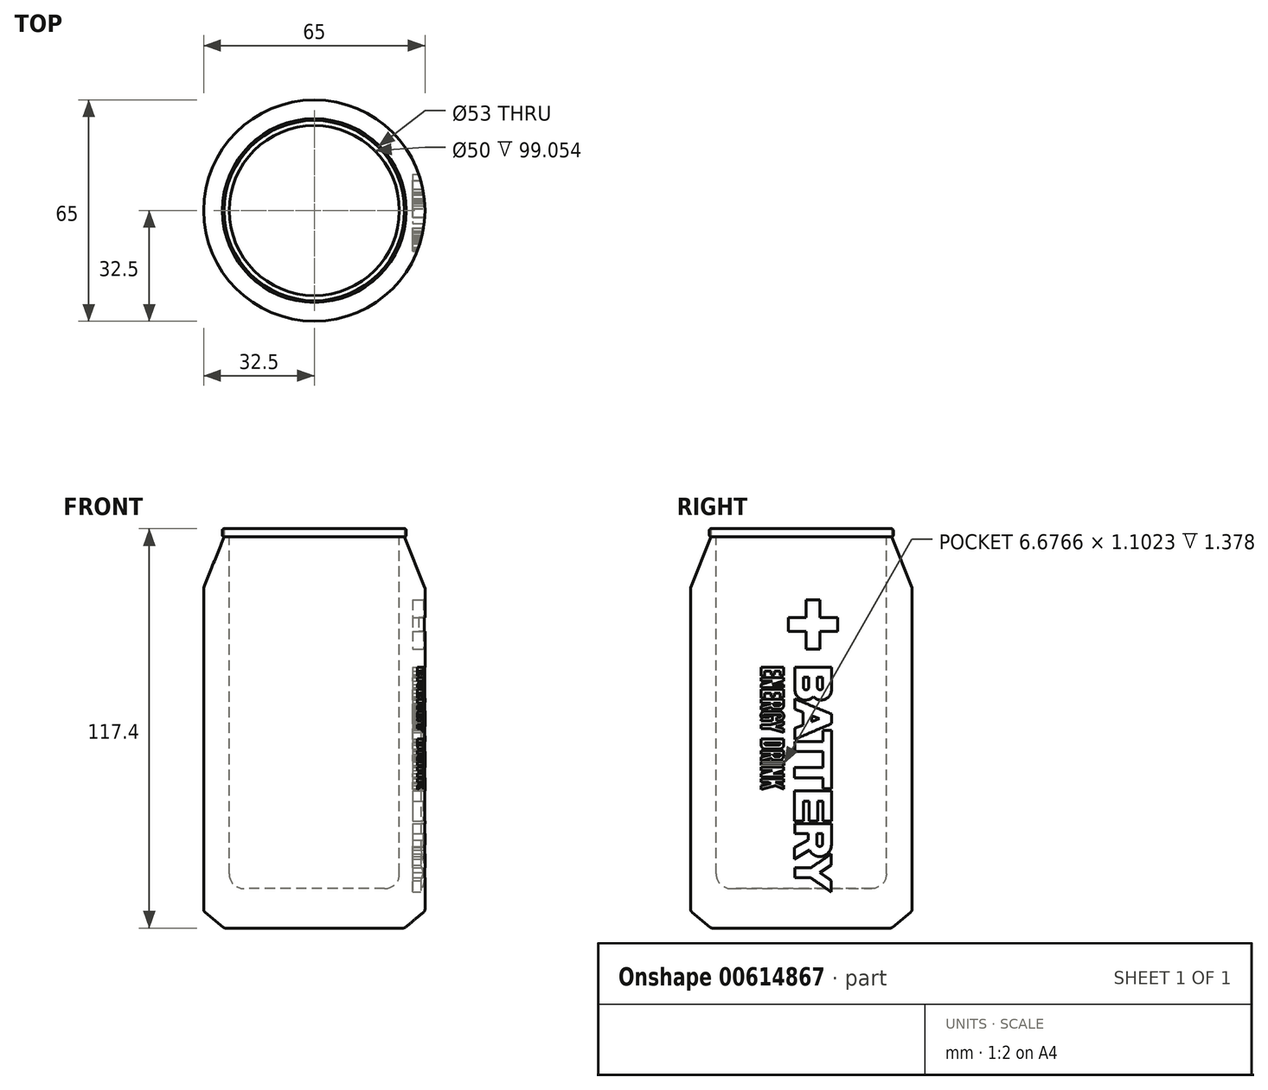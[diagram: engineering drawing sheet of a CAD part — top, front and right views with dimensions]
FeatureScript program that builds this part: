
annotation { "Feature Type Name" : "Feature", "Feature Type Description" : "" }
export const myFeature = defineFeature(function(context is Context, id is Id, definition is map)
    precondition{}
    {
        {
            var Q0;
            Q0=qCreatedBy(makeId("Top.planeOp"),FACE);
            var sketch = newSketch(context, id + "F0", { "sketchPlane" : qUnion([Q0])});
            skCircle(sketch, "E0", {"center": v(0, 0) * mm, "radius": 32.5 * mm});
            skSolve(sketch);
        }
        {
            var Q0;
            Q0=makeQuery(id+"F0.imprint","IMPRINT",FACE,{"disambiguationData":[TD([[makeQuery(id+"F0.imprint","IMPRINT",EDGE,{"derivedFrom":sQuery(id+"F0.wireOp",EDGE,"E0")}),1.0]])]});
            extrude(context, id + "F1", {"entities" : qUnion([Q0]), "depth" : 115 * mm, "offsetDistance" : 25 * mm});
        }
        {
            var Q0;
            Q0=makeQuery(id+"F1.opExtrude","CAP_FACE",FACE,{"disambiguationData":[OSD([sQuery(id+"F0.wireOp",EDGE,"E0")])],"isStart":true});
            chamfer(context, id + "F2", {"entities" : qUnion([Q0]), "chamferType" : ChamferType.TWO_OFFSETS, "width1" : 5 * mm, "oppositeDirection" : false, "width2" : 6 * mm, "tangentPropagation" : true});
        }
        {
            var Q0;
            {var subQ0=sQuery(id+"F0.wireOp",EDGE,"E0");Q0=makeQuery(id+"F2.opChamfer","BLEND_EDGE",EDGE,{"blendedFrom":[makeQuery(id+"F1.opExtrude","CAP_EDGE",EDGE,{"disambiguationData":[OSD([subQ0])],"isStart":true}),makeQuery(id+"F1.opExtrude","SWEPT_FACE",FACE,{"disambiguationData":[OSD([subQ0])]})],"blendedInto":[makeQuery(id+"F1.opExtrude","SWEPT_FACE",FACE,{"disambiguationData":[OSD([subQ0])]})]});}
            var Q1;
            {var subQ0=sQuery(id+"F0.wireOp",EDGE,"E0");Q1=makeQuery(id+"F2.opChamfer","BLEND_EDGE",EDGE,{"blendedFrom":[makeQuery(id+"F1.opExtrude","CAP_EDGE",EDGE,{"disambiguationData":[OSD([subQ0])],"isStart":true}),makeQuery(id+"F1.opExtrude","CAP_FACE",FACE,{"disambiguationData":[OSD([subQ0])],"isStart":true})],"blendedInto":[makeQuery(id+"F1.opExtrude","CAP_FACE",FACE,{"disambiguationData":[OSD([subQ0])],"isStart":true})]});}
            fillet(context, id + "F3", {"entities" : qUnion([Q0, Q1]), "radius" : 1.04 * mm, "tangentPropagation" : true, "allowEdgeOverflow" : false});
        }
        {
            var Q0;
            Q0=makeQuery(id+"F1.opExtrude","CAP_FACE",FACE,{"disambiguationData":[OSD([sQuery(id+"F0.wireOp",EDGE,"E0")])],"isStart":false});
            chamfer(context, id + "F4", {"entities" : qUnion([Q0]), "chamferType" : ChamferType.TWO_OFFSETS, "width1" : 6 * mm, "oppositeDirection" : false, "width2" : 15 * mm, "tangentPropagation" : true});
        }
        {
            var Q0;
            Q0=makeQuery(id+"F1.opExtrude","CAP_FACE",FACE,{"disambiguationData":[OSD([sQuery(id+"F0.wireOp",EDGE,"E0")])],"isStart":false});
            var sketch = newSketch(context, id + "F5", { "sketchPlane" : qUnion([Q0])});
            skCircle(sketch, "E1", {"center": v(0, 0) * mm, "radius": 25 * mm});
            skSolve(sketch);
        }
        {
            var Q0;
            Q0=makeQuery(id+"F5.imprint","IMPRINT",FACE,{"disambiguationData":[TD([[makeQuery(id+"F5.imprint","IMPRINT",EDGE,{"derivedFrom":sQuery(id+"F5.wireOp",EDGE,"E1")}),1.0]])]});
            extrude(context, id + "F6", {"entities" : qUnion([Q0]), "operationType" : NewBodyOperationType.REMOVE, "oppositeDirection" : true, "depth" : 103.4 * mm, "offsetDistance" : 25 * mm});
        }
        {
            var Q0;
            Q0=makeQuery(id+"F1.opExtrude","CAP_FACE",FACE,{"disambiguationData":[OSD([sQuery(id+"F0.wireOp",EDGE,"E0")])],"isStart":false});
            var sketch = newSketch(context, id + "F7", { "sketchPlane" : qUnion([Q0])});
            skCircle(sketch, "E2", {"center": v(0, 0) * mm, "radius": 27 * mm});
            skSolve(sketch);
        }
        {
            var Q0;
            Q0=makeQuery(id+"F7.imprint","IMPRINT",FACE,{"disambiguationData":[TD([[makeQuery(id+"F7.imprint","IMPRINT",EDGE,{"derivedFrom":sQuery(id+"F7.wireOp",EDGE,"E2")}),1.0]])]});
            var Q1;
            Q1=makeQuery(id+"F7.imprint","IMPRINT",FACE,{"disambiguationData":[TD([[makeQuery(id+"F7.imprint","IMPRINT",EDGE,{"derivedFrom":makeQuery(id+"F6.boolean.opBoolean","COPY",EDGE,{"derivedFrom":makeQuery(id+"F6.opExtrude","CAP_EDGE",EDGE,{"disambiguationData":[OSD([sQuery(id+"F5.wireOp",EDGE,"E1")])],"isStart":true})})}),-1.0]])]});
            extrude(context, id + "F8", {"entities" : qUnion([Q0, Q1]), "operationType" : NewBodyOperationType.ADD, "depth" : 2.4 * mm, "offsetDistance" : 25 * mm});
        }
        {
            var Q0;
            Q0=makeQuery(id+"F8.opExtrude","SWEPT_FACE",FACE,{"disambiguationData":[OSD([sQuery(id+"F7.wireOp",EDGE,"E2")])]});
            var Q1;
            Q1=makeQuery(id+"F8.opExtrude","CAP_EDGE",EDGE,{"disambiguationData":[OSD([sQuery(id+"F5.wireOp",EDGE,"E1")])],"isStart":false});
            var Q2;
            {var subQ0=sQuery(id+"F0.wireOp",EDGE,"E0");Q2=makeQuery(id+"F4.opChamfer","BLEND_EDGE",EDGE,{"blendedFrom":[makeQuery(id+"F1.opExtrude","CAP_EDGE",EDGE,{"disambiguationData":[OSD([subQ0])],"isStart":false}),makeQuery(id+"F1.opExtrude","SWEPT_FACE",FACE,{"disambiguationData":[OSD([subQ0])]})],"blendedInto":[makeQuery(id+"F1.opExtrude","SWEPT_FACE",FACE,{"disambiguationData":[OSD([subQ0])]})]});}
            fillet(context, id + "F9", {"entities" : qUnion([Q0, Q1, Q2]), "radius" : .5 * mm, "tangentPropagation" : true, "allowEdgeOverflow" : false});
        }
        {
            var Q0;
            Q0=qCreatedBy(makeId("Right.planeOp"),FACE);
            cPlane(context, id + "F10", {"entities" : qUnion([Q0]), "cplaneType" : CPlaneType.OFFSET, "offset" : 41.2 * mm, "width" : 150 * mm, "height" : 150 * mm});
        }
        {
            var Q0;
            Q0=qCreatedBy(id+"F10.planeOp",FACE);
            var sketch = newSketch(context, id + "F11", { "sketchPlane" : qUnion([Q0])});
            skLineSegment(sketch, "E3", {"start": v(-9.72, 42.86) * mm, "end": v(-11.78, 42.86) * mm});
            skLineSegment(sketch, "E4", {"start": v(-5.14, 41.9) * mm, "end": v(-7.6, 42.86) * mm});
            skLineSegment(sketch, "E5", {"start": v(-5.14, 40.87) * mm, "end": v(-5.14, 41.9) * mm});
            skLineSegment(sketch, "E6", {"start": v(-7.6, 41.85) * mm, "end": v(-5.14, 40.87) * mm});
            skLineSegment(sketch, "E7", {"start": v(-11.8, 40.77) * mm, "end": v(-7.6, 41.85) * mm});
            skLineSegment(sketch, "E8", {"start": v(-11.8, 41.83) * mm, "end": v(-11.8, 40.77) * mm});
            skLineSegment(sketch, "E9", {"start": v(-5.18, 67.76) * mm, "end": v(-6.17, 67.76) * mm});
            skLineSegment(sketch, "E10", {"start": v(-6.17, 69.09) * mm, "end": v(-6.17, 67.76) * mm});
            skLineSegment(sketch, "E11", {"start": v(-5.18, 69.09) * mm, "end": v(-5.18, 67.76) * mm});
            skLineSegment(sketch, "E12", {"start": v(-10.8, 69.09) * mm, "end": v(-8.85, 69.09) * mm});
            skLineSegment(sketch, "E13", {"start": v(-11.82, 70.2) * mm, "end": v(-5.18, 70.2) * mm});
            skLineSegment(sketch, "E14", {"start": v(-5.18, 70.2) * mm, "end": v(-5.18, 69.09) * mm});
            skLineSegment(sketch, "E15", {"start": v(-11.82, 70.2) * mm, "end": v(-11.82, 69.09) * mm});
            skLineSegment(sketch, "E16", {"start": v(-7.83, 75.55) * mm, "end": v(-6.2, 75.55) * mm});
            skLineSegment(sketch, "E17", {"start": v(-11.8, 71.6) * mm, "end": v(-8.5, 72.66) * mm});
            skLineSegment(sketch, "E18", {"start": v(-5.2, 72.66) * mm, "end": v(-8.5, 71.6) * mm});
            skLineSegment(sketch, "E19", {"start": v(-5.2, 70.67) * mm, "end": v(-11.8, 70.67) * mm});
            skLineSegment(sketch, "E20", {"start": v(-5.2, 71.6) * mm, "end": v(-8.5, 71.6) * mm});
            skLineSegment(sketch, "E21", {"start": v(-11.8, 71.6) * mm, "end": v(-11.8, 70.67) * mm});
            skLineSegment(sketch, "E22", {"start": v(-5.2, 71.6) * mm, "end": v(-5.2, 70.67) * mm});
            skLineSegment(sketch, "E23", {"start": v(-11.8, 73.6) * mm, "end": v(-5.2, 73.6) * mm});
            skLineSegment(sketch, "E24", {"start": v(-11.8, 72.66) * mm, "end": v(-8.5, 72.66) * mm});
            skLineSegment(sketch, "E25", {"start": v(-5.2, 72.66) * mm, "end": v(-5.2, 73.6) * mm});
            skLineSegment(sketch, "E26", {"start": v(-11.8, 72.66) * mm, "end": v(-11.8, 73.6) * mm});
            skLineSegment(sketch, "E27", {"start": v(-10.82, 74.14) * mm, "end": v(-11.82, 74.14) * mm});
            skLineSegment(sketch, "E28", {"start": v(-11.82, 75.55) * mm, "end": v(-11.82, 74.14) * mm});
            skLineSegment(sketch, "E29", {"start": v(-10.82, 75.55) * mm, "end": v(-10.82, 74.14) * mm});
            skLineSegment(sketch, "E30", {"start": v(-7.83, 74.54) * mm, "end": v(-8.85, 74.54) * mm});
            skLineSegment(sketch, "E31", {"start": v(-8.85, 75.55) * mm, "end": v(-8.85, 74.54) * mm});
            skLineSegment(sketch, "E32", {"start": v(-7.83, 75.55) * mm, "end": v(-7.83, 74.54) * mm});
            skLineSegment(sketch, "E33", {"start": v(-5.16, 74.18) * mm, "end": v(-6.2, 74.18) * mm});
            skLineSegment(sketch, "E34", {"start": v(-6.2, 75.55) * mm, "end": v(-6.2, 74.18) * mm});
            skLineSegment(sketch, "E35", {"start": v(-5.16, 75.55) * mm, "end": v(-5.16, 74.18) * mm});
            skLineSegment(sketch, "E36", {"start": v(-10.82, 75.55) * mm, "end": v(-8.85, 75.55) * mm});
            skLineSegment(sketch, "E37", {"start": v(-11.82, 76.67) * mm, "end": v(-5.16, 76.67) * mm});
            skLineSegment(sketch, "E38", {"start": v(-5.16, 76.67) * mm, "end": v(-5.16, 75.55) * mm});
            skLineSegment(sketch, "E39", {"start": v(-11.82, 76.67) * mm, "end": v(-11.82, 75.55) * mm});
            skLineSegment(sketch, "E40", {"start": v(8.83, 10.61) * mm, "end": v(2.77, 14.79) * mm});
            skLineSegment(sketch, "E41", {"start": v(8.83, 13.98) * mm, "end": v(8.83, 10.61) * mm});
            skLineSegment(sketch, "E42", {"start": v(5.42, 16.3) * mm, "end": v(8.83, 13.98) * mm});
            skLineSegment(sketch, "E43", {"start": v(8.82, 18.56) * mm, "end": v(5.42, 16.3) * mm});
            skLineSegment(sketch, "E44", {"start": v(8.82, 21.8) * mm, "end": v(8.82, 18.56) * mm});
            skLineSegment(sketch, "E45", {"start": v(2.77, 17.7) * mm, "end": v(8.82, 21.8) * mm});
            skLineSegment(sketch, "E46", {"start": v(-1.93, 14.79) * mm, "end": v(2.77, 14.79) * mm});
            skLineSegment(sketch, "E47", {"start": v(-1.93, 17.7) * mm, "end": v(2.77, 17.7) * mm});
            skLineSegment(sketch, "E48", {"start": v(-1.93, 17.7) * mm, "end": v(-1.93, 14.79) * mm});
            skLineSegment(sketch, "E49", {"start": v(4.8, 37.31) * mm, "end": v(6.33, 37.31) * mm});
            skLineSegment(sketch, "E50", {"start": v(2.04, 27.75) * mm, "end": v(-1.92, 27.75) * mm});
            skArc(sketch, "E51", {"start": v(2.36, 22.94) * mm, "mid": v(6.22, 21.13) * mm, "end": v(8.86, 24.47) * mm});
            skArc(sketch, "E52", {"start": v(4.57, 24.84) * mm, "mid": v(5.42, 23.99) * mm, "end": v(6.28, 24.84) * mm});
            skLineSegment(sketch, "E53", {"start": v(8.86, 27.75) * mm, "end": v(8.86, 24.47) * mm});
            skLineSegment(sketch, "E54", {"start": v(6.28, 27.75) * mm, "end": v(6.28, 24.84) * mm});
            skLineSegment(sketch, "E55", {"start": v(4.57, 27.75) * mm, "end": v(4.57, 24.84) * mm});
            skLineSegment(sketch, "E56", {"start": v(-1.98, 20.3) * mm, "end": v(2.36, 22.94) * mm});
            skLineSegment(sketch, "E57", {"start": v(-1.98, 23.66) * mm, "end": v(-1.98, 20.3) * mm});
            skLineSegment(sketch, "E58", {"start": v(2.04, 25.9) * mm, "end": v(-1.98, 23.66) * mm});
            skLineSegment(sketch, "E59", {"start": v(6.3, 54.86) * mm, "end": v(-1.94, 54.86) * mm});
            skLineSegment(sketch, "E60", {"start": v(-1.94, 54.86) * mm, "end": v(-1.94, 51.9) * mm});
            skLineSegment(sketch, "E61", {"start": v(8.85, 40.97) * mm, "end": v(6.3, 40.97) * mm});
            skLineSegment(sketch, "E62", {"start": v(8.85, 58.09) * mm, "end": v(6.3, 58.09) * mm});
            skLineSegment(sketch, "E63", {"start": v(6.3, 58.09) * mm, "end": v(6.3, 54.86) * mm});
            skLineSegment(sketch, "E64", {"start": v(8.85, 58.09) * mm, "end": v(8.85, 40.97) * mm});
            skLineSegment(sketch, "E65", {"start": v(5.34, 61.55) * mm, "end": v(3.05, 62.44) * mm});
            skLineSegment(sketch, "E66", {"start": v(3.05, 60.66) * mm, "end": v(5.34, 61.55) * mm});
            skLineSegment(sketch, "E67", {"start": v(3.05, 62.44) * mm, "end": v(3.05, 60.66) * mm});
            skLineSegment(sketch, "E68", {"start": v(8.86, 62.9) * mm, "end": v(-1.9, 67.38) * mm});
            skLineSegment(sketch, "E69", {"start": v(8.86, 60.1) * mm, "end": v(8.86, 62.9) * mm});
            skLineSegment(sketch, "E70", {"start": v(-1.9, 55.48) * mm, "end": v(8.86, 60.1) * mm});
            skLineSegment(sketch, "E71", {"start": v(2.16, 73.7) * mm, "end": v(2.16, 70.77) * mm});
            skLineSegment(sketch, "E72", {"start": v(0.63, 73.7) * mm, "end": v(0.63, 70.77) * mm});
            skLineSegment(sketch, "E73", {"start": v(2.16, 73.7) * mm, "end": v(0.63, 73.7) * mm});
            skArc(sketch, "E74", {"start": v(4.76, 70.77) * mm, "mid": v(5.52, 70.01) * mm, "end": v(6.28, 70.77) * mm});
            skArc(sketch, "E75", {"start": v(0.63, 70.77) * mm, "mid": v(1.4, 70.01) * mm, "end": v(2.16, 70.77) * mm});
            skLineSegment(sketch, "E76", {"start": v(-1.9, 67.38) * mm, "end": v(-1.9, 64.33) * mm});
            skLineSegment(sketch, "E77", {"start": v(-1.9, 64.33) * mm, "end": v(0.48, 63.44) * mm});
            skLineSegment(sketch, "E78", {"start": v(0.48, 63.44) * mm, "end": v(0.48, 59.66) * mm});
            skLineSegment(sketch, "E79", {"start": v(0.48, 59.66) * mm, "end": v(-1.9, 58.7) * mm});
            skLineSegment(sketch, "E80", {"start": v(-1.9, 58.7) * mm, "end": v(-1.9, 55.48) * mm});
            skLineSegment(sketch, "E81", {"start": v(6.3, 51.9) * mm, "end": v(-1.94, 51.9) * mm});
            skLineSegment(sketch, "E82", {"start": v(-1.98, 47.19) * mm, "end": v(-1.98, 44.2) * mm});
            skLineSegment(sketch, "E83", {"start": v(6.3, 47.19) * mm, "end": v(-1.98, 47.19) * mm});
            skLineSegment(sketch, "E84", {"start": v(6.3, 44.2) * mm, "end": v(-1.98, 44.2) * mm});
            skLineSegment(sketch, "E85", {"start": v(6.3, 51.9) * mm, "end": v(6.3, 47.19) * mm});
            skLineSegment(sketch, "E86", {"start": v(6.3, 44.2) * mm, "end": v(6.3, 40.97) * mm});
            skLineSegment(sketch, "E87", {"start": v(-1.98, 40.28) * mm, "end": v(-1.98, 37.31) * mm});
            skLineSegment(sketch, "E88", {"start": v(8.85, 40.28) * mm, "end": v(8.85, 37.31) * mm});
            skLineSegment(sketch, "E89", {"start": v(-1.98, 40.28) * mm, "end": v(8.85, 40.28) * mm});
            skLineSegment(sketch, "E90", {"start": v(0.6, 37.31) * mm, "end": v(2.25, 37.31) * mm});
            skLineSegment(sketch, "E91", {"start": v(8.85, 37.31) * mm, "end": v(8.85, 31.42) * mm});
            skLineSegment(sketch, "E92", {"start": v(6.33, 37.31) * mm, "end": v(6.33, 31.42) * mm});
            skLineSegment(sketch, "E93", {"start": v(8.85, 31.42) * mm, "end": v(6.33, 31.42) * mm});
            skLineSegment(sketch, "E94", {"start": v(4.8, 37.31) * mm, "end": v(4.8, 31.42) * mm});
            skLineSegment(sketch, "E95", {"start": v(2.25, 37.31) * mm, "end": v(2.25, 31.42) * mm});
            skLineSegment(sketch, "E96", {"start": v(4.8, 31.42) * mm, "end": v(2.25, 31.42) * mm});
            skLineSegment(sketch, "E97", {"start": v(0.6, 37.31) * mm, "end": v(0.6, 31.43) * mm});
            skLineSegment(sketch, "E98", {"start": v(-1.98, 37.31) * mm, "end": v(-1.98, 31.43) * mm});
            skLineSegment(sketch, "E99", {"start": v(0.6, 31.43) * mm, "end": v(-1.98, 31.43) * mm});
            skLineSegment(sketch, "E100", {"start": v(8.86, 30.65) * mm, "end": v(8.86, 27.75) * mm});
            skLineSegment(sketch, "E101", {"start": v(-1.92, 30.65) * mm, "end": v(-1.92, 27.75) * mm});
            skLineSegment(sketch, "E102", {"start": v(8.86, 30.65) * mm, "end": v(-1.92, 30.65) * mm});
            skLineSegment(sketch, "E103", {"start": v(6.28, 27.75) * mm, "end": v(4.57, 27.75) * mm});
            skLineSegment(sketch, "E104", {"start": v(2.04, 27.75) * mm, "end": v(2.04, 25.9) * mm});
            skLineSegment(sketch, "E105", {"start": v(-7.8, 69.09) * mm, "end": v(-7.8, 68.04) * mm});
            skLineSegment(sketch, "E106", {"start": v(-8.85, 69.09) * mm, "end": v(-8.85, 68.04) * mm});
            skLineSegment(sketch, "E107", {"start": v(-7.8, 68.04) * mm, "end": v(-8.85, 68.04) * mm});
            skLineSegment(sketch, "E108", {"start": v(-10.8, 69.09) * mm, "end": v(-10.8, 67.65) * mm});
            skLineSegment(sketch, "E109", {"start": v(-11.82, 69.13) * mm, "end": v(-11.82, 67.65) * mm});
            skLineSegment(sketch, "E110", {"start": v(-10.8, 67.65) * mm, "end": v(-11.82, 67.65) * mm});
            skLineSegment(sketch, "E111", {"start": v(-7.8, 69.09) * mm, "end": v(-6.17, 69.09) * mm});
            skLineSegment(sketch, "E112", {"start": v(-11.8, 67.21) * mm, "end": v(-11.8, 66.13) * mm});
            skLineSegment(sketch, "E113", {"start": v(-5.19, 67.21) * mm, "end": v(-5.19, 66.13) * mm});
            skLineSegment(sketch, "E114", {"start": v(-11.8, 67.21) * mm, "end": v(-5.19, 67.21) * mm});
            skLineSegment(sketch, "E115", {"start": v(-11.8, 66.13) * mm, "end": v(-9.06, 66.13) * mm});
            skLineSegment(sketch, "E116", {"start": v(-9.06, 66.13) * mm, "end": v(-9.06, 65.87) * mm});
            skLineSegment(sketch, "E117", {"start": v(-9.06, 65.87) * mm, "end": v(-11.8, 65.26) * mm});
            skLineSegment(sketch, "E118", {"start": v(-11.8, 65.26) * mm, "end": v(-11.8, 64.18) * mm});
            skLineSegment(sketch, "E119", {"start": v(-11.8, 64.18) * mm, "end": v(-8.84, 64.86) * mm});
            skLineSegment(sketch, "E120", {"start": v(-6.1, 66.13) * mm, "end": v(-6.1, 65.75) * mm});
            skLineSegment(sketch, "E121", {"start": v(-8.1, 66.13) * mm, "end": v(-8.1, 65.75) * mm});
            skLineSegment(sketch, "E122", {"start": v(-5.19, 66.13) * mm, "end": v(-5.19, 65.41) * mm});
            skLineSegment(sketch, "E123", {"start": v(-6.56, 65.32) * mm, "end": v(-7.58, 65.32) * mm});
            skLineSegment(sketch, "E124", {"start": v(-6.18, 64.29) * mm, "end": v(-7.87, 64.29) * mm});
            skArc(sketch, "E125", {"start": v(-6.56, 65.32) * mm, "mid": v(-6.25, 65.44) * mm, "end": v(-6.1, 65.75) * mm});
            skArc(sketch, "E126", {"start": v(-8.1, 65.75) * mm, "mid": v(-7.94, 65.41) * mm, "end": v(-7.58, 65.32) * mm});
            skArc(sketch, "E127", {"start": v(-6.18, 64.29) * mm, "mid": v(-5.47, 64.66) * mm, "end": v(-5.19, 65.41) * mm});
            skArc(sketch, "E128", {"start": v(-8.84, 64.86) * mm, "mid": v(-8.43, 64.44) * mm, "end": v(-7.87, 64.29) * mm});
            skLineSegment(sketch, "E129", {"start": v(-6.64, 63.74) * mm, "end": v(-10.67, 63.76) * mm});
            skLineSegment(sketch, "E130", {"start": v(-6.37, 62.71) * mm, "end": v(-10.75, 62.73) * mm});
            skLineSegment(sketch, "E131", {"start": v(-7.26, 61.97) * mm, "end": v(-7.26, 60.94) * mm});
            skLineSegment(sketch, "E132", {"start": v(-7.26, 61.97) * mm, "end": v(-6.37, 61.97) * mm});
            skLineSegment(sketch, "E133", {"start": v(-7.26, 60.94) * mm, "end": v(-6.5, 60.94) * mm});
            skLineSegment(sketch, "E134", {"start": v(-8.49, 62.32) * mm, "end": v(-8.49, 60.91) * mm});
            skLineSegment(sketch, "E135", {"start": v(-8.49, 62.32) * mm, "end": v(-9.33, 62.32) * mm});
            skLineSegment(sketch, "E136", {"start": v(-8.49, 60.91) * mm, "end": v(-9.33, 60.91) * mm});
            skLineSegment(sketch, "E137", {"start": v(-9.33, 60.91) * mm, "end": v(-10.75, 60.91) * mm});
            skLineSegment(sketch, "E138", {"start": v(-9.33, 61.98) * mm, "end": v(-10.75, 61.98) * mm});
            skLineSegment(sketch, "E139", {"start": v(-11.79, 61.34) * mm, "end": v(-11.79, 60.91) * mm});
            skLineSegment(sketch, "E140", {"start": v(-11.79, 60.91) * mm, "end": v(-10.75, 60.91) * mm});
            skLineSegment(sketch, "E141", {"start": v(-11.79, 61.34) * mm, "end": v(-11.36, 61.54) * mm});
            skArc(sketch, "E142", {"start": v(-6.37, 61.97) * mm, "mid": v(-6, 62.34) * mm, "end": v(-6.37, 62.71) * mm});
            skArc(sketch, "E143", {"start": v(-6.5, 60.94) * mm, "mid": v(-5.1, 62.42) * mm, "end": v(-6.64, 63.74) * mm});
            skArc(sketch, "E144", {"start": v(-10.67, 63.76) * mm, "mid": v(-11.84, 62.9) * mm, "end": v(-11.36, 61.54) * mm});
            skArc(sketch, "E145", {"start": v(-10.75, 62.73) * mm, "mid": v(-11.13, 62.36) * mm, "end": v(-10.75, 61.98) * mm});
            skLineSegment(sketch, "E146", {"start": v(-8.1, 66.13) * mm, "end": v(-6.1, 66.13) * mm});
            skLineSegment(sketch, "E147", {"start": v(-9.33, 62.32) * mm, "end": v(-9.33, 61.98) * mm});
            skLineSegment(sketch, "E148", {"start": v(-11.8, 59.76) * mm, "end": v(-11.8, 58.62) * mm});
            skLineSegment(sketch, "E149", {"start": v(-11.8, 59.76) * mm, "end": v(-9.14, 59.76) * mm});
            skLineSegment(sketch, "E150", {"start": v(-11.8, 58.62) * mm, "end": v(-9.14, 58.62) * mm});
            skLineSegment(sketch, "E151", {"start": v(-9.14, 59.76) * mm, "end": v(-5.21, 60.8) * mm});
            skLineSegment(sketch, "E152", {"start": v(-5.21, 60.8) * mm, "end": v(-5.21, 59.76) * mm});
            skLineSegment(sketch, "E153", {"start": v(-5.21, 59.76) * mm, "end": v(-7.5, 59.2) * mm});
            skLineSegment(sketch, "E154", {"start": v(-7.5, 59.2) * mm, "end": v(-5.18, 58.56) * mm});
            skLineSegment(sketch, "E155", {"start": v(-5.18, 58.56) * mm, "end": v(-5.18, 57.52) * mm});
            skLineSegment(sketch, "E156", {"start": v(-5.18, 57.52) * mm, "end": v(-9.14, 58.62) * mm});
            skLineSegment(sketch, "E157", {"start": v(-5.18, 55.52) * mm, "end": v(-5.18, 54.48) * mm});
            skLineSegment(sketch, "E158", {"start": v(-11.8, 55.52) * mm, "end": v(-11.8, 54.48) * mm});
            skLineSegment(sketch, "E159", {"start": v(-5.18, 55.52) * mm, "end": v(-11.8, 55.52) * mm});
            skLineSegment(sketch, "E160", {"start": v(-6.1, 54.48) * mm, "end": v(-10.84, 54.48) * mm});
            skLineSegment(sketch, "E161", {"start": v(-6.81, 53.74) * mm, "end": v(-10.15, 53.74) * mm});
            skLineSegment(sketch, "E162", {"start": v(-6.43, 52.67) * mm, "end": v(-10.8, 52.67) * mm});
            skLineSegment(sketch, "E163", {"start": v(-5.18, 54.48) * mm, "end": v(-5.18, 53.81) * mm});
            skLineSegment(sketch, "E164", {"start": v(-11.8, 54.48) * mm, "end": v(-11.8, 53.83) * mm});
            skArc(sketch, "E165", {"start": v(-6.81, 53.74) * mm, "mid": v(-6.3, 53.96) * mm, "end": v(-6.1, 54.48) * mm});
            skArc(sketch, "E166", {"start": v(-10.84, 54.48) * mm, "mid": v(-10.66, 53.96) * mm, "end": v(-10.15, 53.74) * mm});
            skArc(sketch, "E167", {"start": v(-6.43, 52.67) * mm, "mid": v(-5.55, 52.97) * mm, "end": v(-5.18, 53.81) * mm});
            skArc(sketch, "E168", {"start": v(-11.8, 53.83) * mm, "mid": v(-11.51, 53.07) * mm, "end": v(-10.8, 52.67) * mm});
            skLineSegment(sketch, "E169", {"start": v(-5.22, 52.17) * mm, "end": v(-5.22, 51.13) * mm});
            skLineSegment(sketch, "E170", {"start": v(-11.81, 52.17) * mm, "end": v(-11.81, 51.13) * mm});
            skLineSegment(sketch, "E171", {"start": v(-5.22, 52.17) * mm, "end": v(-11.81, 52.17) * mm});
            skLineSegment(sketch, "E172", {"start": v(-6.06, 51.13) * mm, "end": v(-8.1, 51.13) * mm});
            skLineSegment(sketch, "E173", {"start": v(-9.01, 51.13) * mm, "end": v(-9.01, 50.86) * mm});
            skLineSegment(sketch, "E174", {"start": v(-9.01, 50.86) * mm, "end": v(-11.8, 50.27) * mm});
            skLineSegment(sketch, "E175", {"start": v(-11.8, 50.27) * mm, "end": v(-11.8, 49.15) * mm});
            skLineSegment(sketch, "E176", {"start": v(-11.8, 49.15) * mm, "end": v(-8.81, 49.87) * mm});
            skLineSegment(sketch, "E177", {"start": v(-6.06, 51.13) * mm, "end": v(-6.06, 50.82) * mm});
            skLineSegment(sketch, "E178", {"start": v(-8.1, 51.13) * mm, "end": v(-8.1, 50.8) * mm});
            skLineSegment(sketch, "E179", {"start": v(-6.59, 50.36) * mm, "end": v(-7.6, 50.36) * mm});
            skLineSegment(sketch, "E180", {"start": v(-5.22, 51.13) * mm, "end": v(-5.22, 50.64) * mm});
            skArc(sketch, "E181", {"start": v(-6.59, 50.36) * mm, "mid": v(-6.24, 50.5) * mm, "end": v(-6.06, 50.82) * mm});
            skArc(sketch, "E182", {"start": v(-8.1, 50.8) * mm, "mid": v(-7.93, 50.49) * mm, "end": v(-7.6, 50.36) * mm});
            skArc(sketch, "E183", {"start": v(-6.24, 49.31) * mm, "mid": v(-5.5, 49.8) * mm, "end": v(-5.22, 50.64) * mm});
            skLineSegment(sketch, "E184", {"start": v(-6.24, 49.31) * mm, "end": v(-7.78, 49.31) * mm});
            skArc(sketch, "E185", {"start": v(-8.81, 49.87) * mm, "mid": v(-8.37, 49.46) * mm, "end": v(-7.78, 49.31) * mm});
            skLineSegment(sketch, "E186", {"start": v(-9.01, 51.13) * mm, "end": v(-11.81, 51.13) * mm});
            skLineSegment(sketch, "E187", {"start": v(-5.13, 48.87) * mm, "end": v(-5.13, 47.77) * mm});
            skLineSegment(sketch, "E188", {"start": v(-11.81, 48.87) * mm, "end": v(-11.81, 47.77) * mm});
            skLineSegment(sketch, "E189", {"start": v(-5.13, 48.87) * mm, "end": v(-11.81, 48.87) * mm});
            skLineSegment(sketch, "E190", {"start": v(-5.13, 47.77) * mm, "end": v(-11.81, 47.77) * mm});
            skLineSegment(sketch, "E191", {"start": v(-5.19, 47.31) * mm, "end": v(-5.19, 46.36) * mm});
            skLineSegment(sketch, "E192", {"start": v(-11.81, 47.31) * mm, "end": v(-11.81, 46.36) * mm});
            skLineSegment(sketch, "E193", {"start": v(-5.19, 47.31) * mm, "end": v(-11.81, 47.31) * mm});
            skLineSegment(sketch, "E194", {"start": v(-8.5, 46.36) * mm, "end": v(-11.81, 46.36) * mm});
            skLineSegment(sketch, "E195", {"start": v(-11.8, 44.42) * mm, "end": v(-11.8, 45.36) * mm});
            skLineSegment(sketch, "E196", {"start": v(-5.19, 44.42) * mm, "end": v(-5.19, 45.36) * mm});
            skLineSegment(sketch, "E197", {"start": v(-11.8, 44.42) * mm, "end": v(-5.19, 44.42) * mm});
            skLineSegment(sketch, "E198", {"start": v(-8.28, 45.36) * mm, "end": v(-5.19, 45.36) * mm});
            skLineSegment(sketch, "E199", {"start": v(-5.19, 46.36) * mm, "end": v(-8.28, 45.36) * mm});
            skLineSegment(sketch, "E200", {"start": v(-11.8, 45.36) * mm, "end": v(-8.5, 46.36) * mm});
            skLineSegment(sketch, "E201", {"start": v(-5.21, 43.85) * mm, "end": v(-5.21, 42.86) * mm});
            skLineSegment(sketch, "E202", {"start": v(-11.78, 43.85) * mm, "end": v(-11.78, 42.86) * mm});
            skLineSegment(sketch, "E203", {"start": v(-5.21, 43.85) * mm, "end": v(-11.78, 43.85) * mm});
            skLineSegment(sketch, "E204", {"start": v(-5.21, 42.86) * mm, "end": v(-7.6, 42.86) * mm});
            skLineSegment(sketch, "E205", {"start": v(-9.72, 42.86) * mm, "end": v(-9, 42.5) * mm});
            skLineSegment(sketch, "E206", {"start": v(-9, 42.5) * mm, "end": v(-11.8, 41.83) * mm});
            skLineSegment(sketch, "E207", {"start": v(10.67, 91.28) * mm, "end": v(10.67, 87.24) * mm});
            skLineSegment(sketch, "E208", {"start": v(-3.78, 91.28) * mm, "end": v(-3.78, 87.24) * mm});
            skLineSegment(sketch, "E209", {"start": v(10.67, 91.28) * mm, "end": v(5.46, 91.28) * mm});
            skLineSegment(sketch, "E210", {"start": v(10.67, 87.24) * mm, "end": v(5.46, 87.24) * mm});
            skLineSegment(sketch, "E211", {"start": v(5.46, 96.47) * mm, "end": v(5.46, 91.28) * mm});
            skLineSegment(sketch, "E212", {"start": v(1.4, 96.47) * mm, "end": v(1.4, 91.28) * mm});
            skLineSegment(sketch, "E213", {"start": v(5.46, 96.47) * mm, "end": v(1.4, 96.47) * mm});
            skLineSegment(sketch, "E214", {"start": v(5.46, 82.04) * mm, "end": v(1.4, 82.04) * mm});
            skLineSegment(sketch, "E215", {"start": v(5.46, 87.24) * mm, "end": v(5.46, 82.04) * mm});
            skLineSegment(sketch, "E216", {"start": v(1.4, 91.28) * mm, "end": v(-3.78, 91.28) * mm});
            skLineSegment(sketch, "E217", {"start": v(1.4, 87.24) * mm, "end": v(-3.78, 87.24) * mm});
            skLineSegment(sketch, "E218", {"start": v(1.4, 87.24) * mm, "end": v(1.4, 82.04) * mm});
            skLineSegment(sketch, "E219", {"start": v(8.89, 76.61) * mm, "end": v(-1.9, 76.61) * mm});
            skLineSegment(sketch, "E220", {"start": v(-1.9, 76.61) * mm, "end": v(-1.9, 70.11) * mm});
            skLineSegment(sketch, "E221", {"start": v(8.89, 76.61) * mm, "end": v(8.89, 70.11) * mm});
            skArc(sketch, "E222", {"start": v(3.54, 68.05) * mm, "mid": v(6.92, 67.25) * mm, "end": v(8.89, 70.11) * mm});
            skArc(sketch, "E223", {"start": v(-1.9, 70.11) * mm, "mid": v(0.1, 67.2) * mm, "end": v(3.54, 68.05) * mm});
            skLineSegment(sketch, "E224", {"start": v(6.28, 73.7) * mm, "end": v(4.76, 73.7) * mm});
            skLineSegment(sketch, "E225", {"start": v(4.76, 73.7) * mm, "end": v(4.76, 70.77) * mm});
            skLineSegment(sketch, "E226", {"start": v(6.28, 73.7) * mm, "end": v(6.28, 70.77) * mm});
            skSolve(sketch);
        }
        {
            var Q0;
            Q0 = qSketchRegion(id + "F11", true);
            extrude(context, id + "F12", {"entities" : qUnion([Q0]), "operationType" : NewBodyOperationType.REMOVE, "oppositeDirection" : true, "depth" : 12.3 * mm, "offsetDistance" : 25 * mm});
        }
        {
            var Q0;
            Q0=makeQuery(id+"F6.boolean.opBoolean","COPY",EDGE,{"derivedFrom":makeQuery(id+"F6.opExtrude","CAP_EDGE",EDGE,{"disambiguationData":[OSD([sQuery(id+"F5.wireOp",EDGE,"E1")])],"isStart":false})});
            fillet(context, id + "F13", {"entities" : qUnion([Q0]), "radius" : 4.35 * mm, "tangentPropagation" : true, "allowEdgeOverflow" : false});
        }
    });
